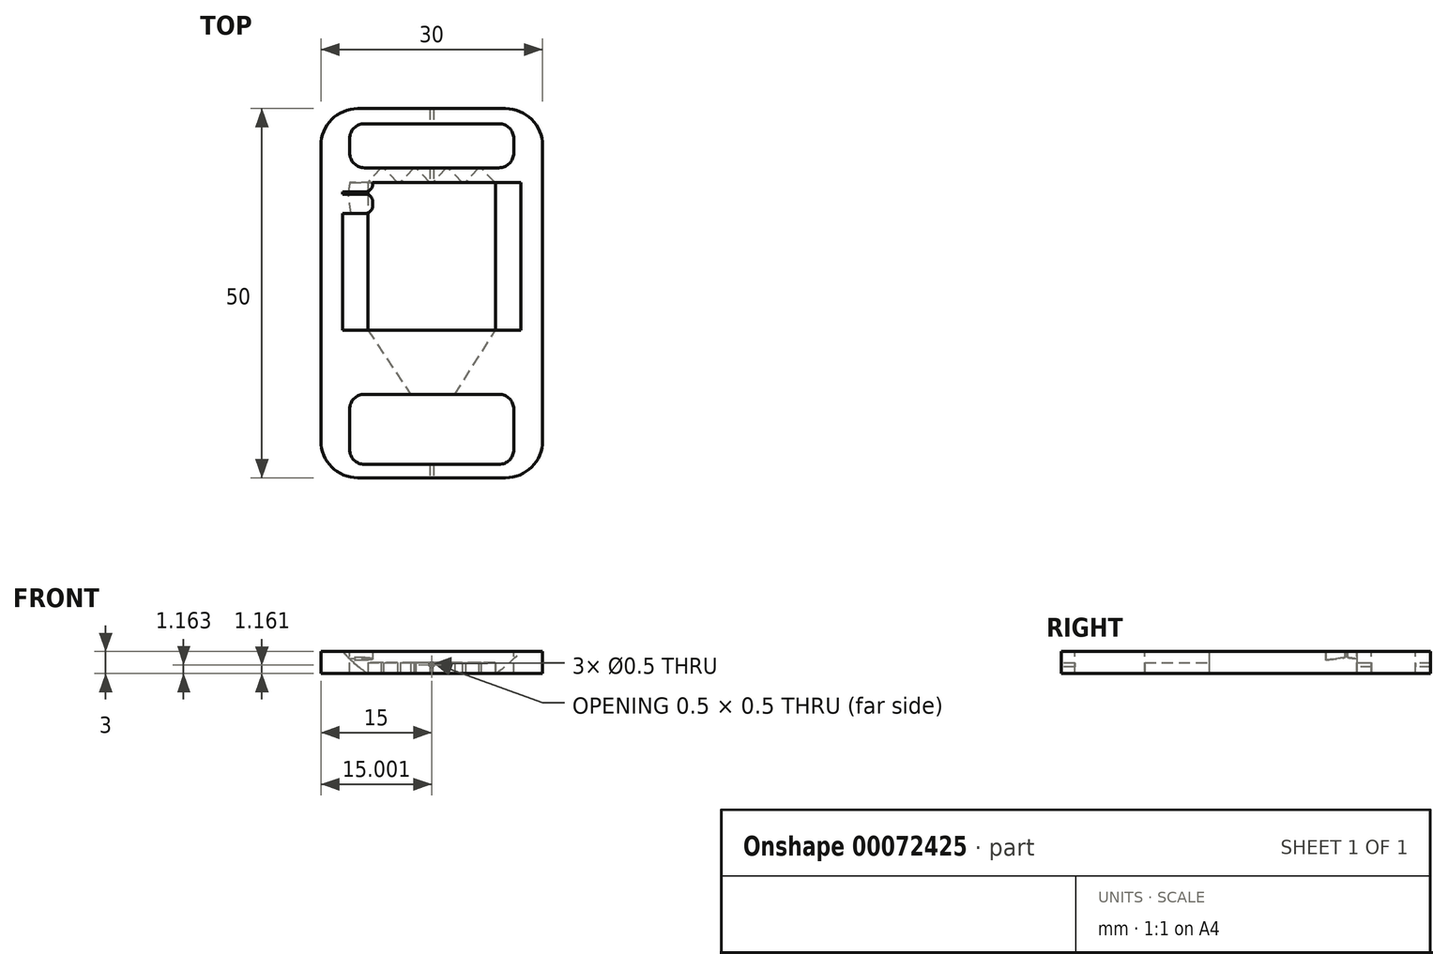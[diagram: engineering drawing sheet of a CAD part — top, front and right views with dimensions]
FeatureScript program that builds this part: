
annotation { "Feature Type Name" : "Feature", "Feature Type Description" : "" }
export const myFeature = defineFeature(function(context is Context, id is Id, definition is map)
    precondition{}
    {
        {
            var Q0;
            Q0=qCreatedBy(makeId("Top.planeOp"),FACE);
            var sketch = newSketch(context, id + "F0", { "sketchPlane" : qUnion([Q0])});
            skLineSegment(sketch, "E0.rect.bottom", {"start": v(10, -25) * mm, "end": v(-10, -25) * mm});
            skLineSegment(sketch, "E0.rect.top", {"start": v(10, 25) * mm, "end": v(-10, 25) * mm});
            skLineSegment(sketch, "E0.rect.left", {"start": v(15, -20) * mm, "end": v(15, 20) * mm});
            skLineSegment(sketch, "E0.rect.right", {"start": v(-15, -20) * mm, "end": v(-15, 20) * mm});
            skPoint(sketch, "E0.rect.middle", {"position": v(0, 0) * mm});
            skPoint(sketch, "E1.visualSharp", {"position": v(-15, 25) * mm});
            skArc(sketch, "E1.filletArc", {"start": v(-10, 25) * mm, "mid": v(-13.54, 23.54) * mm, "end": v(-15, 20) * mm});
            skPoint(sketch, "E2.visualSharp", {"position": v(15, 25) * mm});
            skArc(sketch, "E2.filletArc", {"start": v(15, 20) * mm, "mid": v(13.54, 23.54) * mm, "end": v(10, 25) * mm});
            skPoint(sketch, "E3.visualSharp", {"position": v(15, -25) * mm});
            skArc(sketch, "E3.filletArc", {"start": v(10, -25) * mm, "mid": v(13.54, -23.54) * mm, "end": v(15, -20) * mm});
            skPoint(sketch, "E4.visualSharp", {"position": v(-15, -25) * mm});
            skArc(sketch, "E4.filletArc", {"start": v(-15, -20) * mm, "mid": v(-13.54, -23.54) * mm, "end": v(-10, -25) * mm});
            skSolve(sketch);
        }
        {
            var Q0;
            Q0=qSketchRegion(id+"F0",true);
            extrude(context, id + "F1", {"entities" : qUnion([Q0]), "depth" : 3 * mm});
        }
        {
            var Q0;
            Q0=qCreatedBy(makeId("Front.planeOp"),FACE);
            var sketch = newSketch(context, id + "F2", { "sketchPlane" : qUnion([Q0])});
            skCircle(sketch, "E5", {"center": v(0, 13.2) * mm, "radius": 15.78 * mm});
            skSolve(sketch);
        }
        {
            var Q0;
            Q0=qSketchRegion(id+"F2",true);
            extrude(context, id + "F3", {"entities" : qUnion([Q0]), "operationType" : NewBodyOperationType.REMOVE, "oppositeDirection" : true, "depth" : 15 * mm, "hasSecondDirection" : true, "secondDirectionOppositeDirection" : false, "secondDirectionDepth" : 5 * mm});
        }
        {
            var Q0;
            Q0=makeQuery(id+"F1.opExtrude","CAP_FACE",FACE,{"disambiguationData":[OSD([sQuery(id+"F0.wireOp",EDGE,"E0.rect.bottom"),sQuery(id+"F0.wireOp",EDGE,"E0.rect.top"),sQuery(id+"F0.wireOp",EDGE,"E0.rect.left"),sQuery(id+"F0.wireOp",EDGE,"E0.rect.right")])],"isStart":false});
            var sketch = newSketch(context, id + "F4", { "sketchPlane" : qUnion([Q0])});
            skLineSegment(sketch, "E6.bottom", {"start": v(9.1, -13.68) * mm, "end": v(-9.1, -13.68) * mm});
            skLineSegment(sketch, "E6.top", {"start": v(9.1, -23.18) * mm, "end": v(-9.1, -23.18) * mm});
            skLineSegment(sketch, "E6.left", {"start": v(11.1, -15.68) * mm, "end": v(11.1, -21.18) * mm});
            skLineSegment(sketch, "E6.right", {"start": v(-11.1, -15.68) * mm, "end": v(-11.1, -21.18) * mm});
            skPoint(sketch, "E6.middle", {"position": v(0, -18.43) * mm});
            skLineSegment(sketch, "E7.bottom", {"start": v(9.1, 22.96) * mm, "end": v(-9.1, 22.96) * mm});
            skLineSegment(sketch, "E7.top", {"start": v(9.1, 16.99) * mm, "end": v(-9.1, 16.99) * mm});
            skLineSegment(sketch, "E7.left", {"start": v(11.1, 20.96) * mm, "end": v(11.1, 18.99) * mm});
            skLineSegment(sketch, "E7.right", {"start": v(-11.1, 20.96) * mm, "end": v(-11.1, 18.99) * mm});
            skPoint(sketch, "E7.middle", {"position": v(0, 19.97) * mm});
            skPoint(sketch, "E8.visualSharp", {"position": v(-11.1, -23.18) * mm});
            skArc(sketch, "E8.filletArc", {"start": v(-11.1, -21.18) * mm, "mid": v(-10.52, -22.6) * mm, "end": v(-9.1, -23.18) * mm});
            skPoint(sketch, "E9.visualSharp", {"position": v(-11.1, -13.68) * mm});
            skArc(sketch, "E9.filletArc", {"start": v(-9.1, -13.68) * mm, "mid": v(-10.52, -14.27) * mm, "end": v(-11.1, -15.68) * mm});
            skPoint(sketch, "E10.visualSharp", {"position": v(11.1, -13.68) * mm});
            skArc(sketch, "E10.filletArc", {"start": v(11.1, -15.68) * mm, "mid": v(10.52, -14.27) * mm, "end": v(9.1, -13.68) * mm});
            skPoint(sketch, "E11.visualSharp", {"position": v(11.1, -23.18) * mm});
            skArc(sketch, "E11.filletArc", {"start": v(9.1, -23.18) * mm, "mid": v(10.52, -22.6) * mm, "end": v(11.1, -21.18) * mm});
            skPoint(sketch, "E12.visualSharp", {"position": v(-11.1, 22.96) * mm});
            skArc(sketch, "E12.filletArc", {"start": v(-9.1, 22.96) * mm, "mid": v(-10.52, 22.37) * mm, "end": v(-11.1, 20.96) * mm});
            skPoint(sketch, "E13.visualSharp", {"position": v(-11.1, 16.99) * mm});
            skArc(sketch, "E13.filletArc", {"start": v(-11.1, 18.99) * mm, "mid": v(-10.52, 17.57) * mm, "end": v(-9.1, 16.99) * mm});
            skPoint(sketch, "E14.visualSharp", {"position": v(11.1, 22.96) * mm});
            skArc(sketch, "E14.filletArc", {"start": v(11.1, 20.96) * mm, "mid": v(10.52, 22.37) * mm, "end": v(9.1, 22.96) * mm});
            skPoint(sketch, "E15.visualSharp", {"position": v(11.1, 16.99) * mm});
            skArc(sketch, "E15.filletArc", {"start": v(9.1, 16.99) * mm, "mid": v(10.52, 17.57) * mm, "end": v(11.1, 18.99) * mm});
            skSolve(sketch);
        }
        {
            var Q0;
            Q0=qSketchRegion(id+"F4",true);
            extrude(context, id + "F5", {"entities" : qUnion([Q0]), "operationType" : NewBodyOperationType.REMOVE, "oppositeDirection" : true, "depth" : 25 * mm});
        }
        {
            var Q0;
            Q0=makeQuery(id+"F1.opExtrude","CAP_FACE",FACE,{"disambiguationData":[OSD([sQuery(id+"F0.wireOp",EDGE,"E0.rect.bottom"),sQuery(id+"F0.wireOp",EDGE,"E0.rect.top"),sQuery(id+"F0.wireOp",EDGE,"E0.rect.left"),sQuery(id+"F0.wireOp",EDGE,"E0.rect.right")])],"isStart":true});
            var sketch = newSketch(context, id + "F6", { "sketchPlane" : qUnion([Q0])});
            skLineSegment(sketch, "E16", {"start": v(3.14, 13.68) * mm, "end": v(8.64, 5) * mm});
            skLineSegment(sketch, "E17", {"start": v(8.64, 5) * mm, "end": v(-8.64, 5) * mm});
            skLineSegment(sketch, "E18", {"start": v(-8.64, 5) * mm, "end": v(-2.86, 13.68) * mm});
            skLineSegment(sketch, "E19", {"start": v(-2.86, 13.68) * mm, "end": v(3.14, 13.68) * mm});
            skLineSegment(sketch, "E20", {"start": v(-4.64, -15) * mm, "end": v(-6.53, -16.99) * mm});
            skLineSegment(sketch, "E21", {"start": v(-6.53, -16.99) * mm, "end": v(-6.83, -16.99) * mm});
            skLineSegment(sketch, "E22", {"start": v(-6.83, -16.99) * mm, "end": v(-8.64, -15) * mm});
            skLineSegment(sketch, "E23", {"start": v(-8.64, -15) * mm, "end": v(-4.64, -15) * mm});
            skLineSegment(sketch, "E24", {"start": v(0, 0) * mm, "end": v(0, 27.85) * mm, "construction": true});
            skPoint(sketch, "E24.endSnap0", {"position": v(0, 25) * mm});
            skLineSegment(sketch, "E25", {"start": v(0, 27.85) * mm, "end": v(0, -28.3) * mm, "construction": true});
            skPoint(sketch, "E25.endSnap0", {"position": v(0, -25) * mm});
            skLineSegment(sketch, "E26.1.0.0", {"start": v(-4.24, -15) * mm, "end": v(-0.24, -15) * mm});
            skLineSegment(sketch, "E26.1.0.1", {"start": v(-0.24, -15) * mm, "end": v(-2.13, -16.99) * mm});
            skLineSegment(sketch, "E26.1.0.2", {"start": v(-2.13, -16.99) * mm, "end": v(-2.43, -16.99) * mm});
            skLineSegment(sketch, "E26.1.0.3", {"start": v(-2.43, -16.99) * mm, "end": v(-4.24, -15) * mm});
            skLineSegment(sketch, "E26.2.0.0", {"start": v(0.16, -15) * mm, "end": v(4.16, -15) * mm});
            skLineSegment(sketch, "E26.2.0.1", {"start": v(4.16, -15) * mm, "end": v(2.27, -16.99) * mm});
            skLineSegment(sketch, "E26.2.0.2", {"start": v(2.27, -16.99) * mm, "end": v(1.97, -16.99) * mm});
            skLineSegment(sketch, "E26.2.0.3", {"start": v(1.97, -16.99) * mm, "end": v(0.16, -15) * mm});
            skLineSegment(sketch, "E26.3.0.0", {"start": v(4.56, -15) * mm, "end": v(8.56, -15) * mm});
            skLineSegment(sketch, "E26.3.0.1", {"start": v(8.56, -15) * mm, "end": v(6.67, -16.99) * mm});
            skLineSegment(sketch, "E26.3.0.2", {"start": v(6.67, -16.99) * mm, "end": v(6.37, -16.99) * mm});
            skLineSegment(sketch, "E26.3.0.3", {"start": v(6.37, -16.99) * mm, "end": v(4.56, -15) * mm});
            skLineSegment(sketch, "E26.direction1", {"start": v(-8.64, -15) * mm, "end": v(-4.24, -15) * mm, "construction": true});
            skSolve(sketch);
        }
        {
            var Q0;
            Q0=qSketchRegion(id+"F6",true);
            extrude(context, id + "F7", {"entities" : qUnion([Q0]), "operationType" : NewBodyOperationType.REMOVE, "oppositeDirection" : true, "depth" : 1.5 * mm});
        }
        {
            var Q0;
            Q0=makeQuery(id+"F1.opExtrude","SWEPT_FACE",FACE,{"disambiguationData":[OSD([sQuery(id+"F0.wireOp",EDGE,"E0.rect.right")])]});
            var sketch = newSketch(context, id + "F8", { "sketchPlane" : qUnion([Q0])});
            skLineSegment(sketch, "E27", {"start": v(-16.55, 3) * mm, "end": v(-13.73, 3) * mm});
            skLineSegment(sketch, "E28", {"start": v(-13.73, 3) * mm, "end": v(-13.73, 2.17) * mm});
            skLineSegment(sketch, "E29", {"start": v(-13.73, 2.17) * mm, "end": v(-16.4, 1.76) * mm});
            skLineSegment(sketch, "E30", {"start": v(-16.4, 1.76) * mm, "end": v(-16.55, 3) * mm});
            skLineSegment(sketch, "E31", {"start": v(-13.43, 3) * mm, "end": v(-10.8, 3) * mm});
            skLineSegment(sketch, "E32", {"start": v(-10.8, 3) * mm, "end": v(-10.8, 1.8) * mm});
            skLineSegment(sketch, "E33", {"start": v(-13.43, 3) * mm, "end": v(-13.43, 2.17) * mm});
            skLineSegment(sketch, "E34", {"start": v(-13.43, 2.17) * mm, "end": v(-10.8, 1.8) * mm});
            skSolve(sketch);
        }
        {
            var Q0;
            Q0=qSketchRegion(id+"F8",true);
            extrude(context, id + "F9", {"entities" : qUnion([Q0]), "operationType" : NewBodyOperationType.ADD, "oppositeDirection" : true, "depth" : 7 * mm});
        }
        {
            var Q0;
            Q0=makeQuery(id+"F9.opExtrude","CAP_EDGE",EDGE,{"disambiguationData":[OSD([sQuery(id+"F8.wireOp",EDGE,"E32")])],"isStart":false});
            var Q1;
            Q1=makeQuery(id+"F9.opExtrude","CAP_EDGE",EDGE,{"disambiguationData":[OSD([sQuery(id+"F8.wireOp",EDGE,"E33")])],"isStart":false});
            var Q2;
            Q2=makeQuery(id+"F9.opExtrude","CAP_EDGE",EDGE,{"disambiguationData":[OSD([sQuery(id+"F8.wireOp",EDGE,"E28")])],"isStart":false});
            fillet(context, id + "F10", {"entities" : qUnion([Q0, Q1, Q2]), "radius" : 1 * mm, "tangentPropagation" : true, "allowEdgeOverflow" : false});
        }
        {
            var Q0;
            Q0=makeQuery(id+"F1.opExtrude","SWEPT_FACE",FACE,{"disambiguationData":[OSD([sQuery(id+"F0.wireOp",EDGE,"E0.rect.bottom")])]});
            var sketch = newSketch(context, id + "F11", { "sketchPlane" : qUnion([Q0])});
            skCircle(sketch, "E35", {"center": v(0, 1.16) * mm, "radius": 0.25 * mm});
            skPoint(sketch, "E35.centerSnap0", {"position": v(0, 3) * mm});
            skSolve(sketch);
        }
        {
            var Q0;
            Q0=qSketchRegion(id+"F11",true);
            extrude(context, id + "F12", {"entities" : qUnion([Q0]), "operationType" : NewBodyOperationType.REMOVE, "oppositeDirection" : true, "depth" : 60 * mm});
        }
    });
